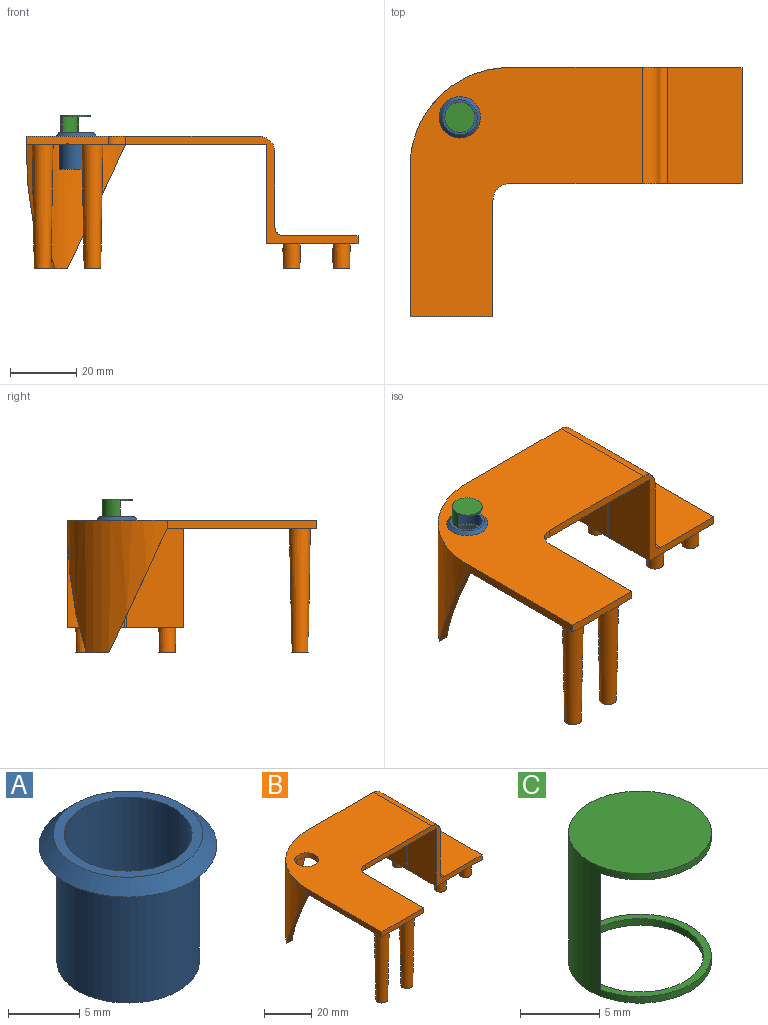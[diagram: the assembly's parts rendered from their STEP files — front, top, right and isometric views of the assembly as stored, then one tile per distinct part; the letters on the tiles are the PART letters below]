
ASSEMBLY  parts=3 mates=2
PART A: 7 faces, bbox 12.5x12.5x11 mm
  f0: cylinder r=4.5mm len=10mm, axis (0,0,1), area 282.7mm2, adj f2,f5
  f1: cylinder r=5mm len=10mm, axis (0,0,1), area 314.2mm2, adj f3,f6
  f2: plane 10.5x10.5mm, normal (0,0,1), area 23mm2, adj f0,f4
  f3: plane 12.5x12.5mm, normal (0,0,-1), area 44.2mm2, adj f1,f4
  f4: cone r=5.25mm half-angle=45deg, axis (0,0,-1), area 51.1mm2, adj f2,f3
  f5: plane 9x9mm, normal (0,0,1), area 63.6mm2, adj f0
  f6: plane 10x10mm, normal (0,0,-1), area 78.5mm2, adj f1
PART B: 48 faces, bbox 100x75x40 mm
  f0: plane 9.52x5.3mm, normal (0,0,-1), area 16.9mm2, adj f37,f38,f45
  f1: plane 22.25x17.25mm, normal (0,0,-1), area 372.5mm2, adj f2,f3,f36,f38,f45
  f2: plane 70x32.5mm, normal (0,1,0), area 245.8mm2, adj f1,f3,f4,f6,f11,f12,f13,f15
  f3: plane 30x17.25mm, normal (-1,0,0), area 517.5mm2, adj f1,f2,f4,f41
  f4: plane 17.25x14.75mm, normal (0,0,-1), area 221.4mm2, adj f2,f3,f31,f42,f43,f44
  f5: plane 25x2.5mm, normal (0,-1,0), area 62.4mm2, adj f6,f7,f8,f13,f19,f40
  f6: plane 75x49.75mm, normal (0,0,-1), area 1275.3mm2, adj f2,f5,f7,f18,f21,f33,f34,f35
  f7: plane 45x2.5mm, normal (-1,0,0), area 112.5mm2, adj f5,f6,f12,f13
  f8: plane 35x2.5mm, normal (1,0,0), area 87.5mm2, adj f5,f9,f13,f19
  f9: cylinder r=5mm len=5mm, axis (0,0,-1), area 19.6mm2, adj f8,f10,f13,f19
  f10: plane 70x32.5mm, normal (0,-1,0), area 246mm2, adj f9,f11,f13,f15,f16,f17,f19,f20
  f11: plane 35x22.5mm, normal (1,0,0), area 787.5mm2, adj f2,f10,f46,f47
  f12: cylinder r=30mm len=40mm, axis (0,0,-1), area 1207.8mm2, adj f2,f7,f13,f14,f34,f35
  f13: plane 75x70mm, normal (0,0,1), area 3183.7mm2, adj f2,f5,f7,f8,f9,f10,f12,f33
  f14: plane 6.87x6.87mm, normal (0,0,-1), area 18.8mm2, adj f12,f18,f34,f35
  f15: plane 35x2.5mm, normal (1,0,0), area 87.5mm2, adj f2,f10,f16,f20
  f16: plane 35x22.5mm, normal (0,0,1), area 787.5mm2, adj f2,f10,f15,f47
  f17: plane 30x17.25mm, normal (-1,0,0), area 517.5mm2, adj f10,f19,f20,f41
  f18: cylinder r=27.5mm len=37.5mm, axis (0,0,-1), area 938.2mm2, adj f6,f14,f34,f35
  f19: plane 59.75x57.25mm, normal (0,0,-1), area 1363.3mm2, adj f5,f8,f9,f10,f17,f23,f38,f39
  f20: plane 35x27.5mm, normal (0,0,-1), area 639.5mm2, adj f2,f10,f15,f17,f25,f27,f29,f42
  f21: cone r=2.5mm half-angle=1deg, axis (0,0,1), area 666.3mm2, adj f6,f22
  f22: plane 5x5mm, normal (0,0,-1), area 19.6mm2, adj f21
  f23: cone r=2.5mm half-angle=1deg, axis (0,0,1), area 666.3mm2, adj f19,f24
  f24: plane 5x5mm, normal (0,0,-1), area 19.6mm2, adj f23
  f25: cone r=2.5mm half-angle=1deg, axis (0,0,1), area 120.9mm2, adj f20,f26
  f26: plane 5x5mm, normal (0,0,-1), area 19.6mm2, adj f25
  f27: cone r=2.5mm half-angle=1deg, axis (0,0,1), area 120.9mm2, adj f20,f28
  f28: plane 5x5mm, normal (0,0,-1), area 19.6mm2, adj f27
  f29: cone r=2.5mm half-angle=1deg, axis (0,0,1), area 120.9mm2, adj f20,f30
  f30: plane 5x5mm, normal (0,0,-1), area 19.6mm2, adj f29
  f31: cone r=2.5mm half-angle=1deg, axis (0,0,1), area 120.9mm2, adj f4,f32
  f32: plane 5x5mm, normal (0,0,-1), area 19.6mm2, adj f31
  f33: cylinder r=5mm len=10mm, axis (0,0,-1), area 78.5mm2, adj f6,f13
  f34: plane 37.5x17.5mm, normal (0,-0.91,-0.42), area 111.3mm2, adj f6,f12,f14,f18
  f35: plane 37.5x17.5mm, normal (0.91,0,-0.42), area 111.3mm2, adj f6,f12,f14,f18
  f36: cylinder r=0.25mm len=10mm, axis (0,-1,0), area 7.9mm2, adj f1,f2,f6,f37,f45
  f37: torus R=7.5mm, axis (0,0,-1), area 7.8mm2, adj f0,f6,f36,f38,f45
  f38: cylinder r=0.25mm len=35.25mm, axis (-1,0,0), area 26mm2, adj f0,f1,f6,f19,f37,f39,f41,f45
  f39: torus R=25mm, axis (0,0,1), area 30.8mm2, adj f6,f19,f38,f40
  f40: cylinder r=0.25mm len=32.5mm, axis (0,-1,0), area 25.5mm2, adj f5,f6,f19,f39
  f41: cylinder r=0.25mm len=30.25mm, axis (0,0,1), area 23.6mm2, adj f3,f17,f38,f44
  f42: cylinder r=0.25mm len=10mm, axis (0,-1,0), area 7.9mm2, adj f2,f4,f20,f43
  f43: torus R=7.5mm, axis (0,0,-1), area 9.3mm2, adj f4,f20,f42,f44
  f44: cylinder r=0.25mm len=7.5mm, axis (-1,0,0), area 5.8mm2, adj f4,f20,f41,f43
  f45: torus R=7.5mm, axis (0,0,1), area 7.8mm2, adj f0,f1,f36,f37,f38
  f46: cylinder r=5mm len=35mm, axis (0,-1,0), area 274.9mm2, adj f2,f10,f11,f13
  f47: cylinder r=2.5mm len=35mm, axis (0,1,0), area 137.4mm2, adj f2,f10,f11,f16
PART C: 8 faces, bbox 9x9x10 mm
  f0: cylinder r=4.5mm len=10mm, axis (0,0,1), area 107.8mm2, adj f2,f3,f4,f5,f6,f7
  f1: cylinder r=4mm len=9.5mm, axis (0,0,1), area 77.1mm2, adj f2,f4,f5,f6,f7
  f2: plane 9x9mm, normal (0,0,-1), area 13.4mm2, adj f0,f1
  f3: plane 9x9mm, normal (0,0,1), area 63.6mm2, adj f0
  f4: plane 8.91x8.91mm, normal (0,0,-1), area 59.6mm2, adj f0,f1,f6,f7
  f5: plane 8.91x8.91mm, normal (0,0,1), area 9.3mm2, adj f0,f1,f6,f7
  f6: plane 9x0.44mm, normal (0.71,-0.71,0), area 5.6mm2, adj f0,f1,f4,f5
  f7: plane 9x0.44mm, normal (0.71,-0.71,0), area 5.6mm2, adj f0,f1,f4,f5
PLACE A at identity
PLACE B at identity fixed
PLACE C t=(0,0,-4.68)mm
MATE fastened A.f0 <-> B.f33  axis (0,0,1) through (-35,22.5,40)mm
MATE slider C.f0 <-> A.f0  axis (0,0,1) through (-35,22.5,46.32)mm
